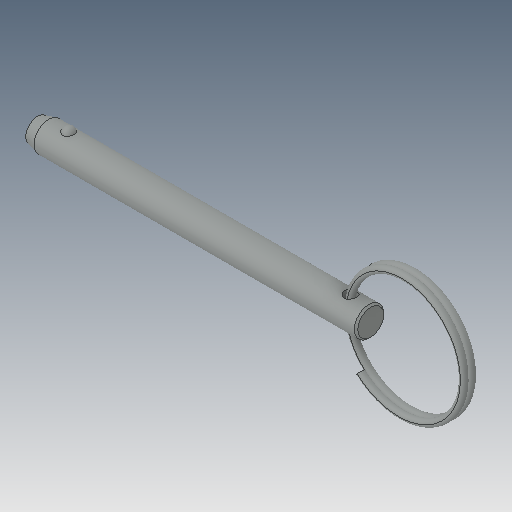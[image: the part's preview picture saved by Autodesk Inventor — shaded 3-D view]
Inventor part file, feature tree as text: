
AUTODESK INVENTOR PART (.ipt)
format: ipt  version: 2023.5 (Build 275446000, 446)  size: 217,088 bytes
history: native  units: in
note: dims shown in document units (in); Inventor stores cm internally (conversion verified against a paired STEP export)
features: revolve x1, other x1, sweep x1
ambient origin geometry x8: Origin, YZ Plane, XZ Plane, XY Plane, X Axis, Y Axis, Z Axis, Center Point
bodies: Solid1 (feature_tree), Solid2 (feature_tree), Solid3 (feature_tree)
feature tree (3):
  revolve  "Revolve2"  [1 undecoded]
  other  "Cut-Revolve2"
  sweep  "Sweep2"
note: 1 required parameter value undecoded (feature->parameter linkage not recoverable at this tier; creation-order binding heuristic only, values carry confidence <= 0.55)
